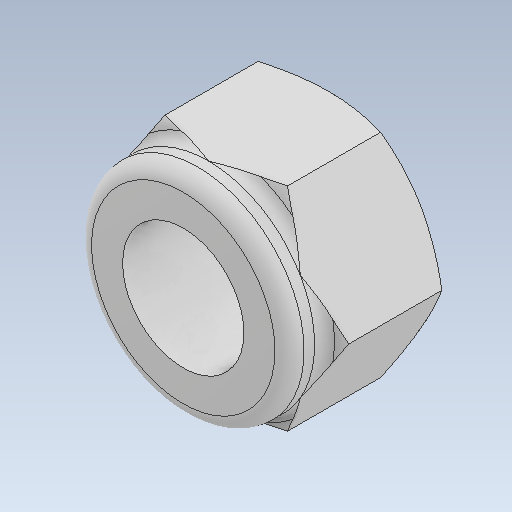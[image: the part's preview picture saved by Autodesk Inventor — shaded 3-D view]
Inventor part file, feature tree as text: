
AUTODESK INVENTOR PART (.ipt)
format: ipt  version: 2020 (Build 240168000, 168)  size: 177,152 bytes
history: native  units: in
note: dims shown in document units (in); Inventor stores cm internally (conversion verified against a paired STEP export)
features: fillet x1
ambient origin geometry x8: Origin, YZ Plane, XZ Plane, XY Plane, X Axis, Y Axis, Z Axis, Center Point
bodies: Solid1 (feature_tree)
feature tree (1):
  fillet  "Fillet7"  [1 undecoded]
note: 1 required parameter value undecoded (feature->parameter linkage not recoverable at this tier; creation-order binding heuristic only, values carry confidence <= 0.55)
